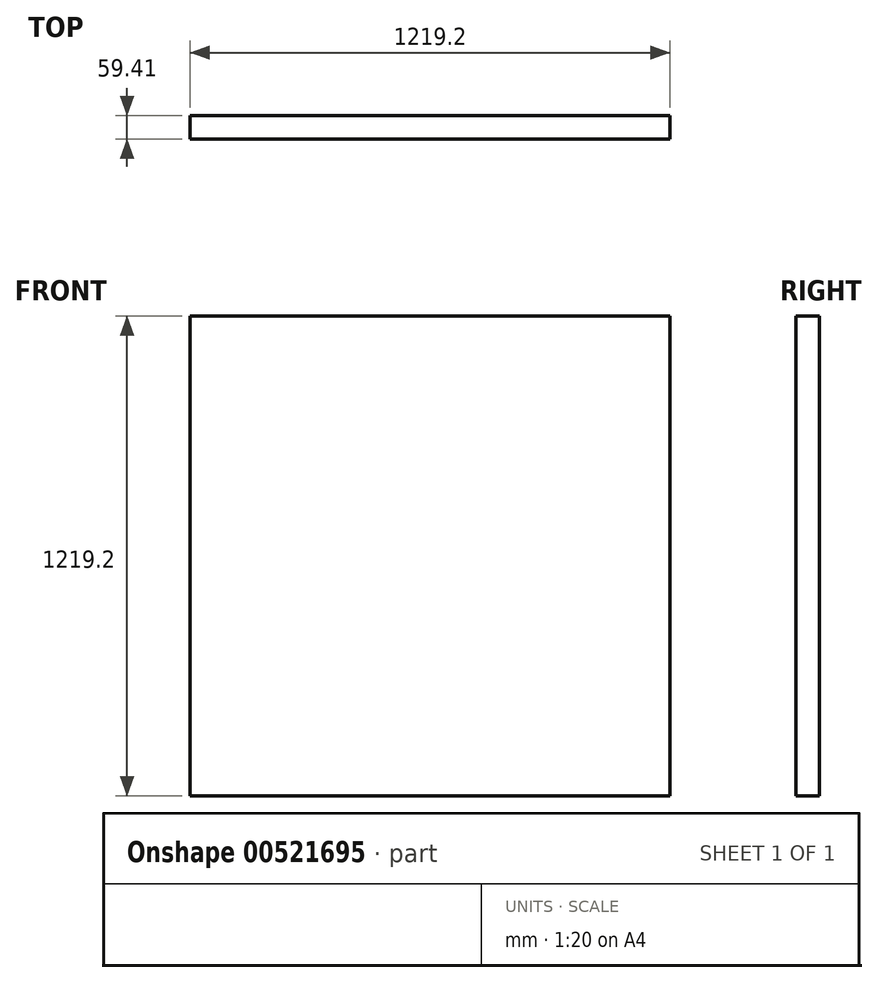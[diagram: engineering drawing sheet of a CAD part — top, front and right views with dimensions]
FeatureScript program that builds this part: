
annotation { "Feature Type Name" : "Feature", "Feature Type Description" : "" }
export const myFeature = defineFeature(function(context is Context, id is Id, definition is map)
    precondition{}
    {
        {
            var Q0;
            Q0=qCreatedBy(makeId("Front.planeOp"),FACE);
            var sketch = newSketch(context, id + "F0", { "sketchPlane" : qUnion([Q0])});
            skLineSegment(sketch, "E0.bottom", {"start": v(609.6, 609.6) * mm, "end": v(-609.6, 609.6) * mm});
            skLineSegment(sketch, "E0.top", {"start": v(609.6, -609.6) * mm, "end": v(-609.6, -609.6) * mm});
            skLineSegment(sketch, "E0.left", {"start": v(609.6, 609.6) * mm, "end": v(609.6, -609.6) * mm});
            skLineSegment(sketch, "E0.right", {"start": v(-609.6, 609.6) * mm, "end": v(-609.6, -609.6) * mm});
            skPoint(sketch, "E0.middle", {"position": v(0, 0) * mm});
            skSolve(sketch);
        }
        {
            var Q0;
            Q0 = qSketchRegion(id + "F0", true);
            extrude(context, id + "F1", {"entities" : qUnion([Q0]), "depth" : 59.4 * mm, "offsetDistance" : 25.4 * mm});
        }
    });
